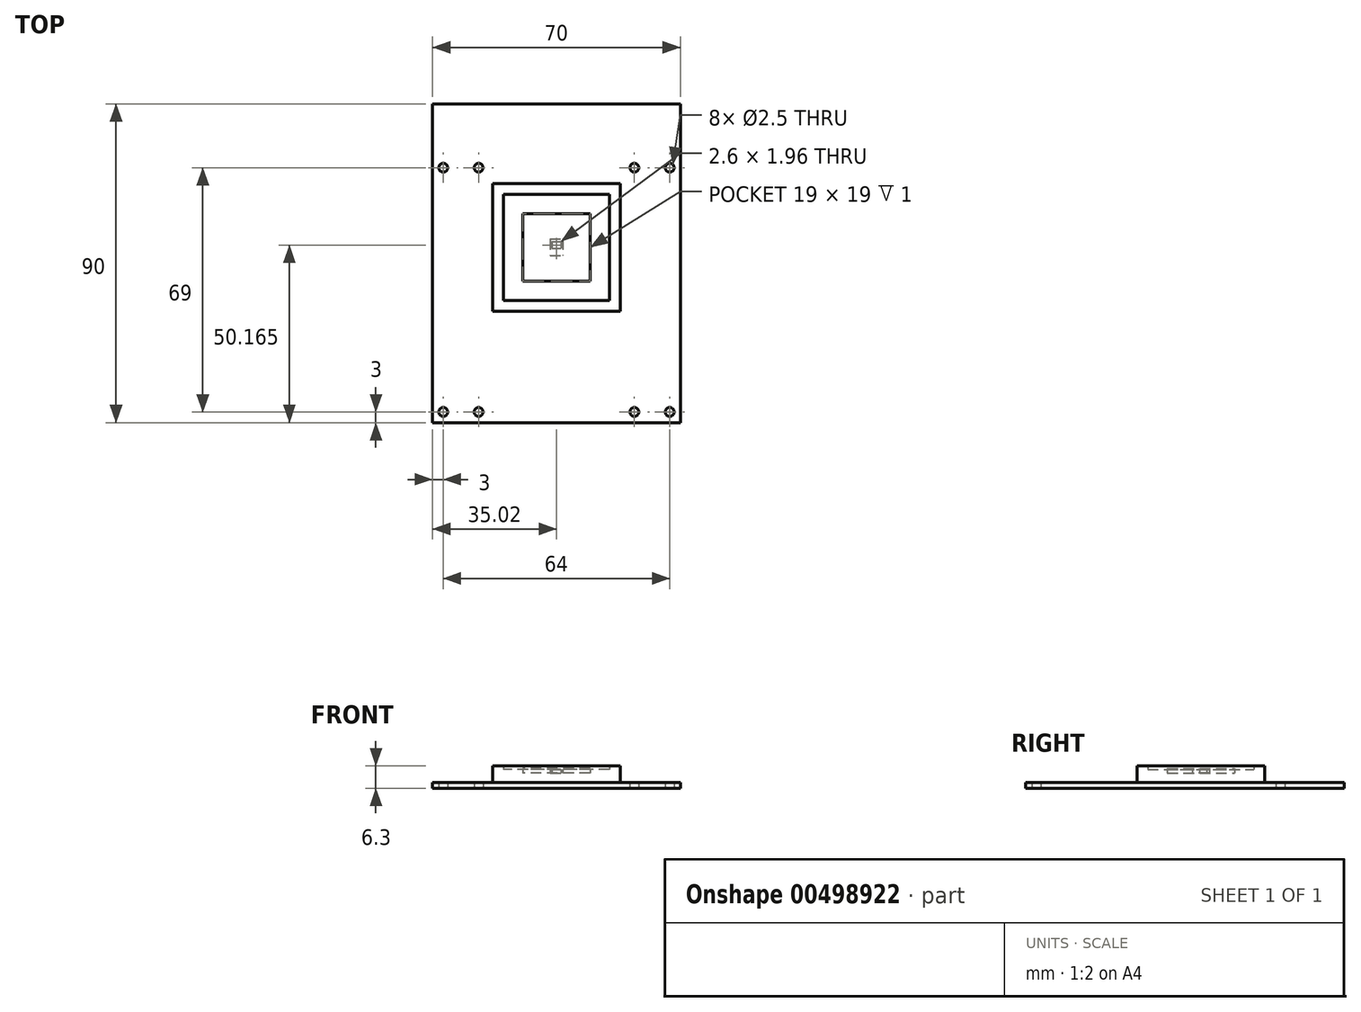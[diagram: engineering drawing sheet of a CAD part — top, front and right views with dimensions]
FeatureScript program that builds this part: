
annotation { "Feature Type Name" : "Feature", "Feature Type Description" : "" }
export const myFeature = defineFeature(function(context is Context, id is Id, definition is map)
    precondition{}
    {
        {
            var Q0;
            Q0=qCreatedBy(makeId("Top.planeOp"),FACE);
            var sketch = newSketch(context, id + "F0", { "sketchPlane" : qUnion([Q0])});
            skLineSegment(sketch, "E0.bottom", {"start": v(-1.83, 2.38) * mm, "end": v(1.83, 2.38) * mm, "construction": true});
            skLineSegment(sketch, "E0.top", {"start": v(-1.83, -2.37) * mm, "end": v(1.83, -2.37) * mm, "construction": true});
            skLineSegment(sketch, "E0.left", {"start": v(-1.83, 2.38) * mm, "end": v(-1.83, -2.37) * mm, "construction": true});
            skLineSegment(sketch, "E0.right", {"start": v(1.83, 2.38) * mm, "end": v(1.83, -2.37) * mm, "construction": true});
            skLineSegment(sketch, "E1.bottom", {"start": v(-1.28, 1.65) * mm, "end": v(1.32, 1.65) * mm, "construction": true});
            skLineSegment(sketch, "E1.top", {"start": v(-1.28, -0.31) * mm, "end": v(1.32, -0.31) * mm, "construction": true});
            skLineSegment(sketch, "E1.left", {"start": v(-1.28, 1.65) * mm, "end": v(-1.28, -0.31) * mm, "construction": true});
            skLineSegment(sketch, "E1.right", {"start": v(1.32, 1.65) * mm, "end": v(1.32, -0.31) * mm, "construction": true});
            skLineSegment(sketch, "E2", {"start": v(-1.28, 1.65) * mm, "end": v(1.32, -0.31) * mm, "construction": true});
            skLineSegment(sketch, "E3", {"start": v(1.32, 1.65) * mm, "end": v(-1.28, -0.31) * mm, "construction": true});
            skPoint(sketch, "E4", {"position": v(0.02, 0.67) * mm});
            skLineSegment(sketch, "E5.bottom", {"start": v(35, -49.5) * mm, "end": v(-35, -49.5) * mm, "construction": true});
            skLineSegment(sketch, "E5.top", {"start": v(35, 40.5) * mm, "end": v(-35, 40.5) * mm, "construction": true});
            skLineSegment(sketch, "E5.left", {"start": v(35, -49.5) * mm, "end": v(35, 40.5) * mm, "construction": true});
            skLineSegment(sketch, "E5.right", {"start": v(-35, -49.5) * mm, "end": v(-35, 40.5) * mm, "construction": true});
            skPoint(sketch, "E5.middle", {"position": v(0, 0) * mm});
            skLineSegment(sketch, "E6.bottom", {"start": v(18, -18) * mm, "end": v(-18, -18) * mm, "construction": true});
            skLineSegment(sketch, "E6.top", {"start": v(18, 18) * mm, "end": v(-18, 18) * mm, "construction": true});
            skLineSegment(sketch, "E6.left", {"start": v(18, -18) * mm, "end": v(18, 18) * mm, "construction": true});
            skLineSegment(sketch, "E6.right", {"start": v(-18, -18) * mm, "end": v(-18, 18) * mm, "construction": true});
            skPoint(sketch, "E7", {"position": v(-32, -46.5) * mm});
            skPoint(sketch, "E8", {"position": v(-22, -46.5) * mm});
            skPoint(sketch, "E9", {"position": v(22, -46.5) * mm});
            skPoint(sketch, "E10", {"position": v(32, -46.5) * mm});
            skPoint(sketch, "E11", {"position": v(32, 22.5) * mm});
            skPoint(sketch, "E12", {"position": v(22, 22.5) * mm});
            skPoint(sketch, "E12.positionSnap0", {"position": v(18, 0) * mm});
            skPoint(sketch, "E13", {"position": v(-22, 22.5) * mm});
            skPoint(sketch, "E14", {"position": v(-32, 22.5) * mm});
            skCircle(sketch, "E15", {"center": v(-32, 22.5) * mm, "radius": 1.25 * mm, "construction": true});
            skCircle(sketch, "E16", {"center": v(-22, 22.5) * mm, "radius": 1.25 * mm, "construction": true});
            skCircle(sketch, "E17", {"center": v(22, 22.5) * mm, "radius": 1.25 * mm, "construction": true});
            skCircle(sketch, "E18", {"center": v(32, 22.5) * mm, "radius": 1.25 * mm, "construction": true});
            skCircle(sketch, "E19", {"center": v(-32, -46.5) * mm, "radius": 1.25 * mm, "construction": true});
            skCircle(sketch, "E20", {"center": v(22, -46.5) * mm, "radius": 1.25 * mm, "construction": true});
            skCircle(sketch, "E21", {"center": v(32, -46.5) * mm, "radius": 1.25 * mm, "construction": true});
            skCircle(sketch, "E22", {"center": v(-22, -46.5) * mm, "radius": 1.25 * mm, "construction": true});
            skLineSegment(sketch, "E23.bottom", {"start": v(15, -15) * mm, "end": v(-15, -15) * mm, "construction": true});
            skLineSegment(sketch, "E23.top", {"start": v(15, 15) * mm, "end": v(-15, 15) * mm, "construction": true});
            skLineSegment(sketch, "E23.left", {"start": v(15, -15) * mm, "end": v(15, 15) * mm, "construction": true});
            skLineSegment(sketch, "E23.right", {"start": v(-15, -15) * mm, "end": v(-15, 15) * mm, "construction": true});
            skLineSegment(sketch, "E24.bottom", {"start": v(9.5, -9.5) * mm, "end": v(-9.5, -9.5) * mm, "construction": true});
            skLineSegment(sketch, "E24.top", {"start": v(9.5, 9.5) * mm, "end": v(-9.5, 9.5) * mm, "construction": true});
            skLineSegment(sketch, "E24.left", {"start": v(9.5, -9.5) * mm, "end": v(9.5, 9.5) * mm, "construction": true});
            skLineSegment(sketch, "E24.right", {"start": v(-9.5, -9.5) * mm, "end": v(-9.5, 9.5) * mm, "construction": true});
            skSolve(sketch);
        }
        {
            var Q0;
            Q0=qCreatedBy(makeId("Top.planeOp"),FACE);
            var sketch = newSketch(context, id + "F1", { "sketchPlane" : qUnion([Q0])});
            skLineSegment(sketch, "E25.0", {"start": v(-35, -49.5) * mm, "end": v(-35, 40.5) * mm});
            skLineSegment(sketch, "E26.0", {"start": v(35, 40.5) * mm, "end": v(-35, 40.5) * mm});
            skLineSegment(sketch, "E27.0", {"start": v(35, -49.5) * mm, "end": v(35, 40.5) * mm});
            skLineSegment(sketch, "E28.0", {"start": v(35, -49.5) * mm, "end": v(-35, -49.5) * mm});
            skCircle(sketch, "E29.0", {"center": v(-32, -46.5) * mm, "radius": 1.25 * mm});
            skPoint(sketch, "E30.0", {"position": v(32, -46.5) * mm});
            skCircle(sketch, "E31.0", {"center": v(22, -46.5) * mm, "radius": 1.25 * mm});
            skCircle(sketch, "E31.1", {"center": v(32, -46.5) * mm, "radius": 1.25 * mm});
            skCircle(sketch, "E32.0", {"center": v(-32, 22.5) * mm, "radius": 1.25 * mm});
            skCircle(sketch, "E32.1", {"center": v(-22, 22.5) * mm, "radius": 1.25 * mm});
            skCircle(sketch, "E33.0", {"center": v(22, 22.5) * mm, "radius": 1.25 * mm});
            skCircle(sketch, "E33.1", {"center": v(32, 22.5) * mm, "radius": 1.25 * mm});
            skCircle(sketch, "E34.0", {"center": v(-22, -46.5) * mm, "radius": 1.25 * mm});
            skSolve(sketch);
        }
        {
            var Q0;
            Q0=makeQuery(id+"F1.imprint","IMPRINT",FACE,{"disambiguationData":[TD([[makeQuery(id+"F1.imprint","IMPRINT",EDGE,{"derivedFrom":sQuery(id+"F1.wireOp",EDGE,"E25.0")}),-1.0]])]});
            extrude(context, id + "F2", {"entities" : qUnion([Q0]), "depth" : 1.65 * mm});
        }
        {
            var Q0;
            Q0=makeQuery(id+"F2.opExtrude","CAP_FACE",FACE,{"disambiguationData":[OSD([sQuery(id+"F1.wireOp",EDGE,"E25.0"),sQuery(id+"F1.wireOp",EDGE,"E26.0"),sQuery(id+"F1.wireOp",EDGE,"E27.0"),sQuery(id+"F1.wireOp",EDGE,"E28.0"),sQuery(id+"F1.wireOp",EDGE,"E31.0"),sQuery(id+"F1.wireOp",EDGE,"E31.1"),sQuery(id+"F1.wireOp",EDGE,"E32.0"),sQuery(id+"F1.wireOp",EDGE,"E32.1"),sQuery(id+"F1.wireOp",EDGE,"E33.0"),sQuery(id+"F1.wireOp",EDGE,"E33.1"),sQuery(id+"F1.wireOp",EDGE,"E34.0"),sQuery(id+"F1.wireOp",EDGE,"E29.0")])],"isStart":false});
            var sketch = newSketch(context, id + "F3", { "sketchPlane" : qUnion([Q0])});
            skLineSegment(sketch, "E35.0", {"start": v(18, 18) * mm, "end": v(-18, 18) * mm});
            skLineSegment(sketch, "E36.0", {"start": v(-18, -18) * mm, "end": v(-18, 18) * mm});
            skLineSegment(sketch, "E37.0", {"start": v(18, -18) * mm, "end": v(-18, -18) * mm});
            skLineSegment(sketch, "E38.0", {"start": v(18, -18) * mm, "end": v(18, 18) * mm});
            skLineSegment(sketch, "E39.0", {"start": v(15, 15) * mm, "end": v(-15, 15) * mm});
            skPoint(sketch, "E40.0", {"position": v(-15, 0) * mm});
            skLineSegment(sketch, "E41.0", {"start": v(-15, -15) * mm, "end": v(-15, 15) * mm});
            skLineSegment(sketch, "E42.0", {"start": v(15, -15) * mm, "end": v(-15, -15) * mm});
            skLineSegment(sketch, "E43.0", {"start": v(15, -15) * mm, "end": v(15, 15) * mm});
            skSolve(sketch);
        }
        {
            var Q0;
            Q0=makeQuery(id+"F3.imprint","IMPRINT",FACE,{"disambiguationData":[TD([[makeQuery(id+"F3.imprint","IMPRINT",EDGE,{"derivedFrom":sQuery(id+"F3.wireOp",EDGE,"E35.0")}),1.0]])]});
            extrude(context, id + "F4", {"entities" : qUnion([Q0]), "depth" : 4.65 * mm});
        }
        {
            var Q0;
            Q0=makeQuery(id+"F3.imprint","IMPRINT",FACE,{"disambiguationData":[TD([[makeQuery(id+"F3.imprint","IMPRINT",EDGE,{"derivedFrom":sQuery(id+"F3.wireOp",EDGE,"E39.0")}),1.0]])]});
            extrude(context, id + "F5", {"entities" : qUnion([Q0]), "operationType" : NewBodyOperationType.ADD, "depth" : 0.5 * mm});
        }
        {
            var Q0;
            Q0=makeQuery(id+"F5.opExtrude","CAP_FACE",FACE,{"disambiguationData":[OSD([sQuery(id+"F3.wireOp",EDGE,"E39.0"),sQuery(id+"F3.wireOp",EDGE,"E41.0"),sQuery(id+"F3.wireOp",EDGE,"E42.0"),sQuery(id+"F3.wireOp",EDGE,"E43.0")])],"isStart":false});
            var sketch = newSketch(context, id + "F6", { "sketchPlane" : qUnion([Q0])});
            skLineSegment(sketch, "E44.0.0", {"start": v(-15, -15) * mm, "end": v(15, -15) * mm});
            skLineSegment(sketch, "E44.0.1", {"start": v(15, -15) * mm, "end": v(15, 15) * mm});
            skLineSegment(sketch, "E44.0.2", {"start": v(15, 15) * mm, "end": v(-15, 15) * mm});
            skLineSegment(sketch, "E44.0.3", {"start": v(-15, 15) * mm, "end": v(-15, -15) * mm});
            skLineSegment(sketch, "E45.0", {"start": v(-9.5, -9.5) * mm, "end": v(-9.5, 9.5) * mm});
            skLineSegment(sketch, "E46.0", {"start": v(9.5, 9.5) * mm, "end": v(-9.5, 9.5) * mm});
            skLineSegment(sketch, "E47.0", {"start": v(9.5, -9.5) * mm, "end": v(9.5, 9.5) * mm});
            skLineSegment(sketch, "E48.0", {"start": v(9.5, -9.5) * mm, "end": v(-9.5, -9.5) * mm});
            skSolve(sketch);
        }
        {
            var Q0;
            Q0=makeQuery(id+"F6.imprint","IMPRINT",FACE,{"disambiguationData":[TD([[makeQuery(id+"F6.imprint","IMPRINT",EDGE,{"derivedFrom":sQuery(id+"F6.wireOp",EDGE,"E44.0.0")}),-1.0]])]});
            extrude(context, id + "F7", {"entities" : qUnion([Q0]), "depth" : (4.65 - 1 - 0.5) * mm});
        }
        {
            var Q0;
            Q0=makeQuery(id+"F6.imprint","IMPRINT",FACE,{"disambiguationData":[TD([[makeQuery(id+"F6.imprint","IMPRINT",EDGE,{"derivedFrom":sQuery(id+"F6.wireOp",EDGE,"E45.0")}),-1.0]])]});
            extrude(context, id + "F8", {"entities" : qUnion([Q0]), "operationType" : NewBodyOperationType.ADD, "depth" : (4.65 - 1 - 0.5 - 1) * mm});
        }
        {
            var Q0;
            Q0=makeQuery(id+"F8.opExtrude","CAP_FACE",FACE,{"disambiguationData":[OSD([sQuery(id+"F6.wireOp",EDGE,"E45.0"),sQuery(id+"F6.wireOp",EDGE,"E46.0"),sQuery(id+"F6.wireOp",EDGE,"E47.0"),sQuery(id+"F6.wireOp",EDGE,"E48.0")])],"isStart":false});
            var sketch = newSketch(context, id + "F9", { "sketchPlane" : qUnion([Q0])});
            skLineSegment(sketch, "E49.0", {"start": v(-1.83, 2.38) * mm, "end": v(-1.83, -2.37) * mm});
            skLineSegment(sketch, "E50.0", {"start": v(-1.83, 2.38) * mm, "end": v(1.83, 2.38) * mm});
            skLineSegment(sketch, "E51.0", {"start": v(1.83, 2.38) * mm, "end": v(1.83, -2.37) * mm});
            skLineSegment(sketch, "E52.0", {"start": v(-1.83, -2.37) * mm, "end": v(1.83, -2.37) * mm});
            skLineSegment(sketch, "E53.0", {"start": v(-1.28, 1.65) * mm, "end": v(-1.28, -0.31) * mm});
            skPoint(sketch, "E54.0", {"position": v(0.02, 1.65) * mm});
            skLineSegment(sketch, "E55.0", {"start": v(1.32, 1.65) * mm, "end": v(1.32, -0.31) * mm});
            skLineSegment(sketch, "E56.0", {"start": v(-1.28, -0.31) * mm, "end": v(1.32, -0.31) * mm});
            skLineSegment(sketch, "E57.0", {"start": v(-1.28, 1.65) * mm, "end": v(1.32, 1.65) * mm});
            skPoint(sketch, "E58.0", {"position": v(0.02, 0.67) * mm});
            skSolve(sketch);
        }
        {
            var Q0;
            Q0=makeQuery(id+"F9.imprint","IMPRINT",FACE,{"disambiguationData":[TD([[makeQuery(id+"F9.imprint","IMPRINT",EDGE,{"derivedFrom":sQuery(id+"F9.wireOp",EDGE,"E49.0")}),1.0]])]});
            extrude(context, id + "F10", {"entities" : qUnion([Q0]), "depth" : 1 * mm});
        }
        {
            var Q0;
            Q0=makeQuery(id+"F9.imprint","IMPRINT",FACE,{"disambiguationData":[TD([[makeQuery(id+"F9.imprint","IMPRINT",EDGE,{"derivedFrom":sQuery(id+"F9.wireOp",EDGE,"E53.0")}),1.0]])]});
            extrude(context, id + "F11", {"entities" : qUnion([Q0]), "depth" : 1 * mm});
        }
        {
            var Q0;
            Q0=makeQuery(id+"F9.imprint","IMPRINT",FACE,{"disambiguationData":[TD([[makeQuery(id+"F9.imprint","IMPRINT",EDGE,{"derivedFrom":sQuery(id+"F9.wireOp",EDGE,"E49.0")}),-1.0]])]});
            var sketch = newSketch(context, id + "F12", { "sketchPlane" : qUnion([Q0])});
            skLineSegment(sketch, "E59.0.0", {"start": v(-9.5, -9.5) * mm, "end": v(9.5, -9.5) * mm});
            skLineSegment(sketch, "E59.0.1", {"start": v(9.5, -9.5) * mm, "end": v(9.5, 9.5) * mm});
            skLineSegment(sketch, "E59.0.2", {"start": v(9.5, 9.5) * mm, "end": v(-9.5, 9.5) * mm});
            skLineSegment(sketch, "E59.0.3", {"start": v(-9.5, 9.5) * mm, "end": v(-9.5, -9.5) * mm});
            skSolve(sketch);
        }
        {
            var Q0;
            Q0 = qSketchRegion(id + "F12", true);
            extrude(context, id + "F13", {"entities" : qUnion([Q0]), "depth" : 1.3 * mm});
        }
    });
